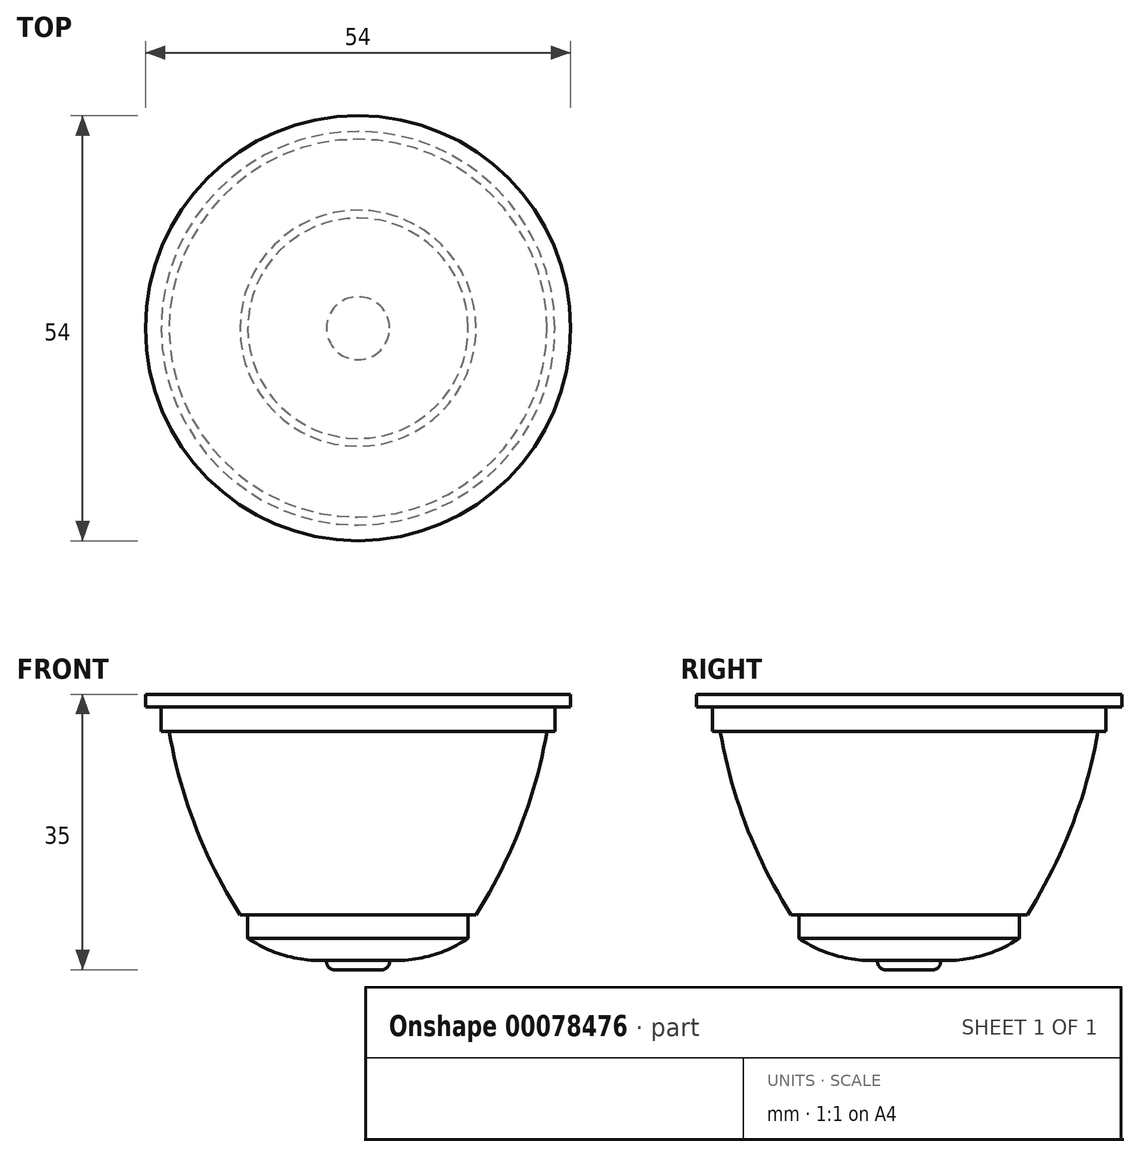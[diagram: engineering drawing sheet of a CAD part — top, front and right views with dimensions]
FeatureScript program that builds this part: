
annotation { "Feature Type Name" : "Feature", "Feature Type Description" : "" }
export const myFeature = defineFeature(function(context is Context, id is Id, definition is map)
    precondition{}
    {
        {
            var Q0;
            Q0=qCreatedBy(makeId("Front.planeOp"),FACE);
            var sketch = newSketch(context, id + "F0", { "sketchPlane" : qUnion([Q0])});
            skLineSegment(sketch, "E0", {"start": v(0, 0) * mm, "end": v(0, 35) * mm});
            skLineSegment(sketch, "E1", {"start": v(0, 0) * mm, "end": v(3, 0) * mm});
            skLineSegment(sketch, "E2", {"start": v(14, 4) * mm, "end": v(14, 7) * mm});
            skLineSegment(sketch, "E3", {"start": v(14, 7) * mm, "end": v(15, 7) * mm});
            skLineSegment(sketch, "E4", {"start": v(24, 30.26) * mm, "end": v(25, 30.26) * mm});
            skLineSegment(sketch, "E5", {"start": v(25, 30.26) * mm, "end": v(25, 33.4) * mm});
            skLineSegment(sketch, "E6", {"start": v(25, 33.4) * mm, "end": v(27, 33.4) * mm});
            skLineSegment(sketch, "E7", {"start": v(27, 33.4) * mm, "end": v(27, 35) * mm});
            skLineSegment(sketch, "E8", {"start": v(27, 35) * mm, "end": v(0, 35) * mm});
            skLineSegment(sketch, "E9", {"start": v(4, 1) * mm, "end": v(4, 1.19) * mm});
            skArc(sketch, "E10", {"start": v(4, 1.19) * mm, "mid": v(9.22, 1.8) * mm, "end": v(14, 4) * mm});
            skArc(sketch, "E11", {"start": v(15, 7) * mm, "mid": v(20.65, 18.18) * mm, "end": v(24, 30.26) * mm});
            skPoint(sketch, "E12.visualSharp", {"position": v(4, 0) * mm});
            skArc(sketch, "E12.filletArc", {"start": v(3, 0) * mm, "mid": v(3.7, 0.3) * mm, "end": v(4, 1) * mm});
            skSolve(sketch);
        }
        {
            var Q0;
            Q0=makeQuery(id+"F0.imprint","IMPRINT",FACE,{"disambiguationData":[TD([[makeQuery(id+"F0.imprint","IMPRINT",EDGE,{"derivedFrom":sQuery(id+"F0.wireOp",EDGE,"E0")}),-1.0]])]});
            var Q1;
            Q1=sQuery(id+"F0.wireOp",EDGE,"E0");
            revolve(context, id + "F1", {"entities" : qUnion([Q0]), "axis" : qUnion([Q1]), "revolveType" : RevolveType.FULL});
        }
    });
